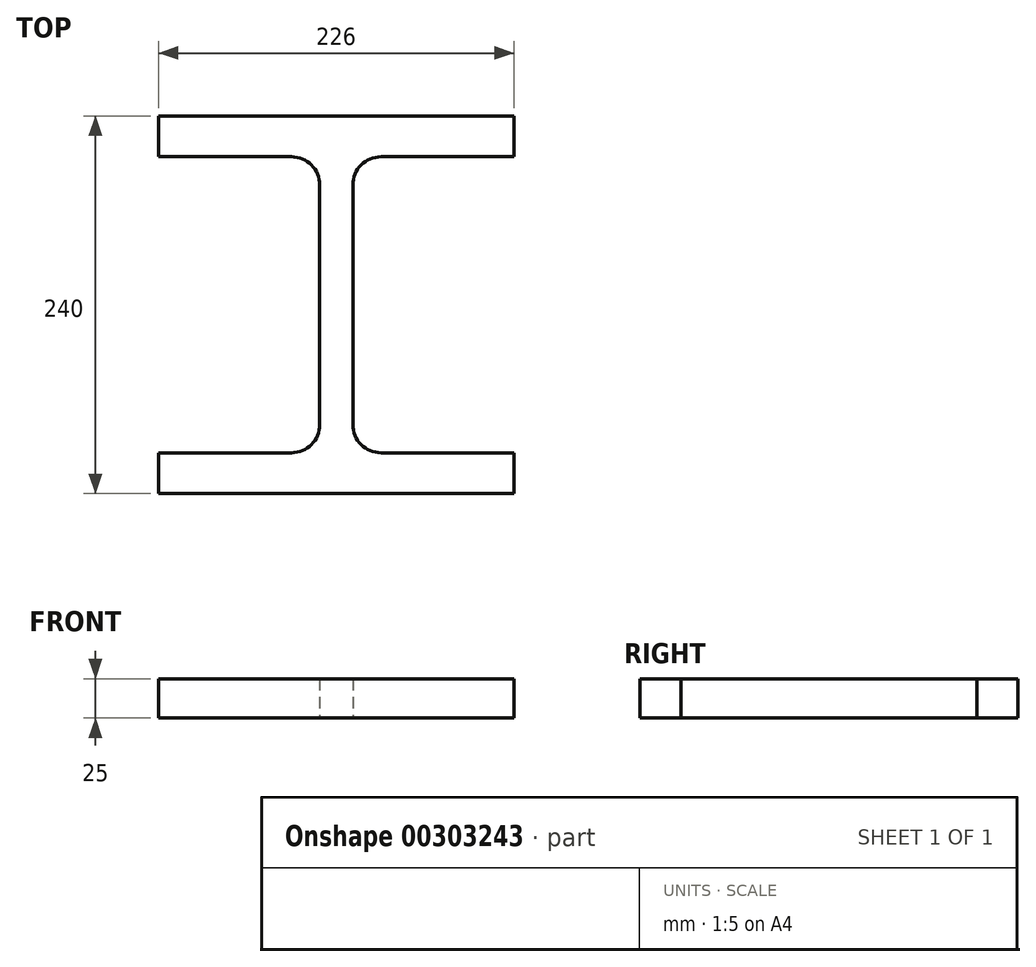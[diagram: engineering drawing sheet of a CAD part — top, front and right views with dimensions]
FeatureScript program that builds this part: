
annotation { "Feature Type Name" : "Feature", "Feature Type Description" : "" }
export const myFeature = defineFeature(function(context is Context, id is Id, definition is map)
    precondition{}
    {
        {
            var Q0;
            Q0=qCreatedBy(makeId("Top.planeOp"),FACE);
            var sketch = newSketch(context, id + "F0", { "sketchPlane" : qUnion([Q0])});
            skLineSegment(sketch, "E0.bottom", {"start": v(-118.25, 128.53) * mm, "end": v(107.75, 128.53) * mm});
            skLineSegment(sketch, "E0.top", {"start": v(-118.25, -111.47) * mm, "end": v(107.75, -111.47) * mm});
            skLineSegment(sketch, "E0.left", {"start": v(-118.25, 128.53) * mm, "end": v(-118.25, 102.53) * mm});
            skLineSegment(sketch, "E0.right", {"start": v(107.75, 128.53) * mm, "end": v(107.75, 102.53) * mm});
            skPoint(sketch, "E1", {"position": v(-118.25, 102.53) * mm});
            skPoint(sketch, "E2", {"position": v(-118.25, -85.47) * mm});
            skPoint(sketch, "E3", {"position": v(107.75, -85.47) * mm});
            skPoint(sketch, "E4", {"position": v(107.75, 102.53) * mm});
            skLineSegment(sketch, "E5", {"start": v(107.75, -111.47) * mm, "end": v(107.75, -85.47) * mm});
            skLineSegment(sketch, "E6", {"start": v(-118.25, -111.47) * mm, "end": v(-118.25, -85.47) * mm});
            skLineSegment(sketch, "E7", {"start": v(5.25, -67.47) * mm, "end": v(5.25, 84.53) * mm});
            skLineSegment(sketch, "E8", {"start": v(-15.75, 84.53) * mm, "end": v(-15.75, -67.47) * mm});
            skLineSegment(sketch, "E9", {"start": v(-15.75, 0) * mm, "end": v(5.25, 0) * mm});
            skLineSegment(sketch, "E10", {"start": v(-118.25, 102.53) * mm, "end": v(-33.75, 102.53) * mm});
            skLineSegment(sketch, "E11", {"start": v(107.75, -85.47) * mm, "end": v(23.25, -85.47) * mm});
            skPoint(sketch, "E12.orphan", {"position": v(0, 128.53) * mm});
            skLineSegment(sketch, "E13.trimOffspring", {"start": v(23.25, 102.53) * mm, "end": v(107.75, 102.53) * mm});
            skPoint(sketch, "E14.end.orphan", {"position": v(0, -111.47) * mm});
            skLineSegment(sketch, "E15.trimOffspring", {"start": v(-33.75, -85.47) * mm, "end": v(-118.25, -85.47) * mm});
            skPoint(sketch, "E16.orphan", {"position": v(-15.75, -111.47) * mm});
            skLineSegment(sketch, "E17.trimOffspring", {"start": v(107.75, -85.47) * mm, "end": v(107.75, -111.47) * mm});
            skLineSegment(sketch, "E18.trimOffspring", {"start": v(-118.25, -85.47) * mm, "end": v(-118.25, -111.47) * mm});
            skPoint(sketch, "E19.visualSharp", {"position": v(5.25, 102.53) * mm});
            skPoint(sketch, "E20.visualSharp", {"position": v(-15.75, -85.47) * mm});
            skPoint(sketch, "E21.visualSharp", {"position": v(5.25, -85.47) * mm});
            skPoint(sketch, "E22.visualSharp", {"position": v(-15.75, 102.53) * mm});
            skLineSegment(sketch, "E23", {"start": v(-15.75, 102.53) * mm, "end": v(-15.75, 84.53) * mm});
            skLineSegment(sketch, "E24", {"start": v(5.25, 102.53) * mm, "end": v(5.25, 84.53) * mm});
            skLineSegment(sketch, "E25", {"start": v(-15.75, -85.47) * mm, "end": v(-15.75, -67.47) * mm});
            skLineSegment(sketch, "E26", {"start": v(5.25, -85.47) * mm, "end": v(5.25, -67.47) * mm});
            skPoint(sketch, "E27.newPointA", {"position": v(-12.75, 102.53) * mm});
            skArc(sketch, "E27.filletArc", {"start": v(-15.75, 84.53) * mm, "mid": v(-21.02, 97.26) * mm, "end": v(-33.75, 102.53) * mm});
            skPoint(sketch, "E28.newPointA", {"position": v(2.25, 102.53) * mm});
            skArc(sketch, "E28.filletArc", {"start": v(23.25, 102.53) * mm, "mid": v(10.52, 97.26) * mm, "end": v(5.25, 84.53) * mm});
            skPoint(sketch, "E29.newPointB", {"position": v(2.25, -85.47) * mm});
            skArc(sketch, "E29.filletArc", {"start": v(5.25, -67.47) * mm, "mid": v(10.52, -80.2) * mm, "end": v(23.25, -85.47) * mm});
            skPoint(sketch, "E30.newPointB", {"position": v(-12.75, -85.47) * mm});
            skArc(sketch, "E30.filletArc", {"start": v(-33.75, -85.47) * mm, "mid": v(-21.02, -80.2) * mm, "end": v(-15.75, -67.47) * mm});
            skSolve(sketch);
        }
        {
            var Q0;
            Q0 = qSketchRegion(id + "F0", true);
            extrude(context, id + "F1", {"entities" : qUnion([Q0]), "depth" : 25 * mm});
        }
    });
